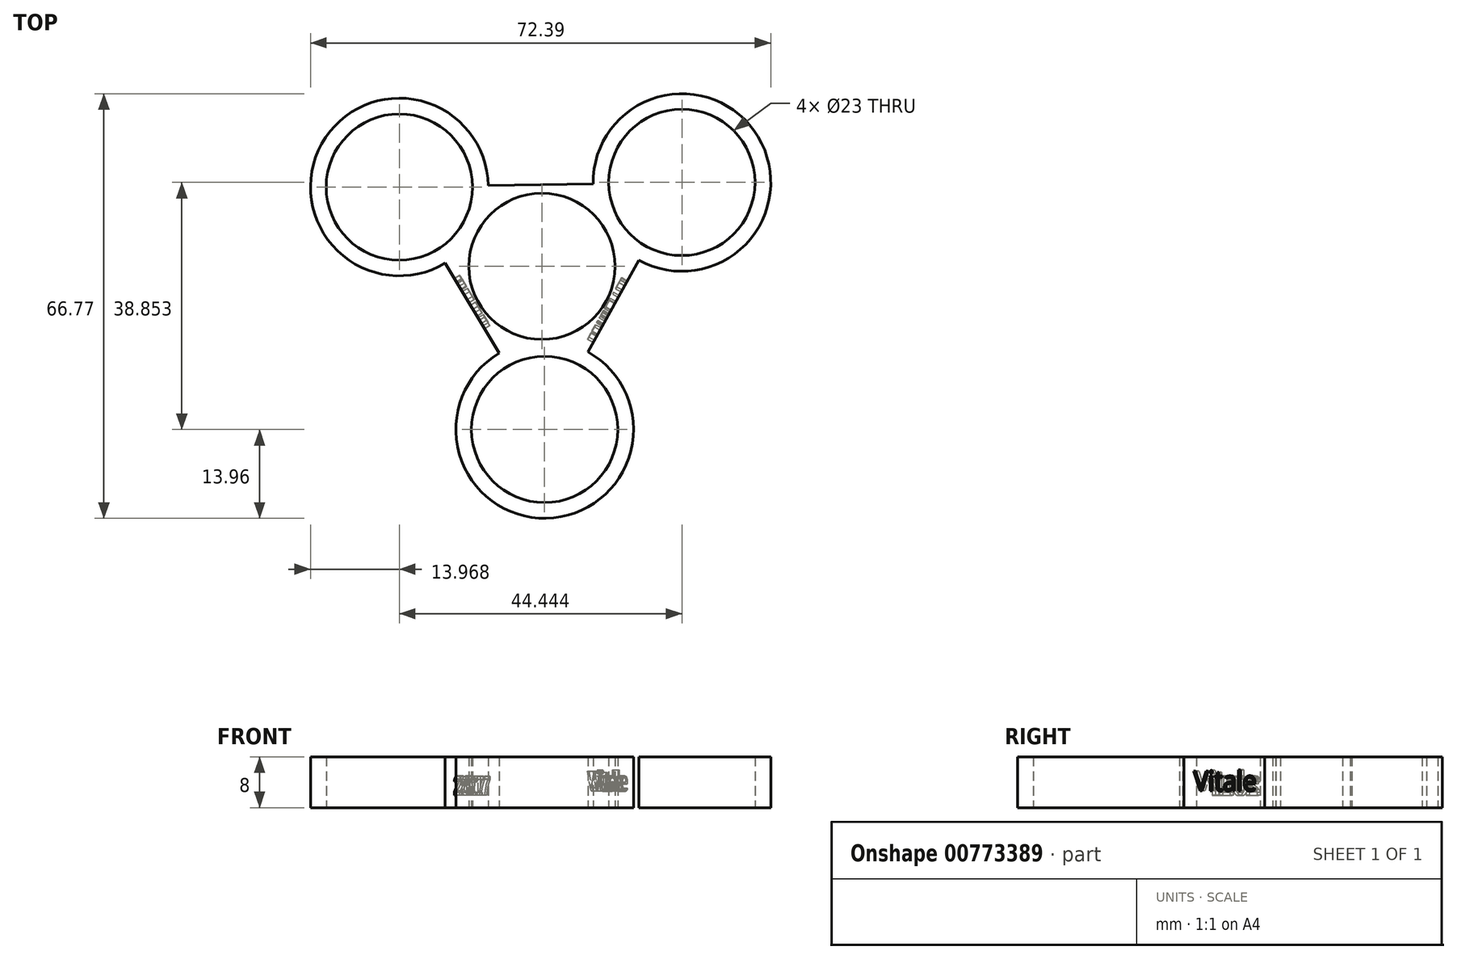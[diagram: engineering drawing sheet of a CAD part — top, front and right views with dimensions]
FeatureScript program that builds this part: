
annotation { "Feature Type Name" : "Feature", "Feature Type Description" : "" }
export const myFeature = defineFeature(function(context is Context, id is Id, definition is map)
    precondition{}
    {
        {
            var Q0;
            Q0=qCreatedBy(makeId("Top.planeOp"),FACE);
            var sketch = newSketch(context, id + "F0", { "sketchPlane" : qUnion([Q0])});
            skCircle(sketch, "E0", {"center": v(0.42, -25.66) * mm, "radius": 11.5 * mm});
            skCircle(sketch, "E1", {"center": v(-22.43, 12.47) * mm, "radius": 11.5 * mm});
            skCircle(sketch, "E2", {"center": v(22.01, 13.2) * mm, "radius": 11.5 * mm});
            skCircle(sketch, "E3", {"center": v(0, 0) * mm, "radius": 11.5 * mm});
            skSolve(sketch);
        }
        {
            var Q0;
            Q0=qCreatedBy(makeId("Top.planeOp"),FACE);
            var sketch = newSketch(context, id + "F1", { "sketchPlane" : qUnion([Q0])});
            skCircle(sketch, "E4", {"center": v(-22.43, 12.47) * mm, "radius": 13.97 * mm});
            skCircle(sketch, "E5", {"center": v(22.02, 13.18) * mm, "radius": 13.97 * mm});
            skCircle(sketch, "E6", {"center": v(0.43, -25.65) * mm, "radius": 13.97 * mm});
            skLineSegment(sketch, "E7", {"start": v(-22.43, 12.47) * mm, "end": v(0.43, -25.65) * mm});
            skLineSegment(sketch, "E8", {"start": v(0.43, -25.65) * mm, "end": v(22.02, 13.18) * mm});
            skLineSegment(sketch, "E9", {"start": v(22.02, 13.18) * mm, "end": v(-22.43, 12.47) * mm});
            skSolve(sketch);
        }
        {
            var Q0;
            Q0 = qSketchRegion(id + "F1", true);
            extrude(context, id + "F2", {"entities" : qUnion([Q0]), "endBound" : BoundingType.SYMMETRIC, "depth" : 8 * mm, "offsetDistance" : 25.4 * mm});
        }
        {
            var Q0;
            Q0 = qSketchRegion(id + "F0", true);
            extrude(context, id + "F3", {"entities" : qUnion([Q0]), "operationType" : NewBodyOperationType.REMOVE, "endBound" : BoundingType.SYMMETRIC, "depth" : 8 * mm, "offsetDistance" : 25.4 * mm});
        }
        {
            var Q0;
            Q0=makeQuery(id+"F2.opExtrude","SWEPT_FACE",FACE,{"disambiguationData":[OSD([sQuery(id+"F1.wireOp",EDGE,"E8")])]});
            var sketch = newSketch(context, id + "F4", { "sketchPlane" : qUnion([Q0])});
            skText(sketch, "E10", { "text": "Vitale", "fontName": "OpenSans-Regular.ttf"});
            const initialGuessF4  = {"E10": [-0.00653, -0.00136, 1, 0, 0.00316]};
            skSetInitialGuess(sketch, initialGuessF4);
            skSolve(sketch);
        }
        {
            var Q0;
            Q0 = qSketchRegion(id + "F4", true);
            extrude(context, id + "F5", {"entities" : qUnion([Q0]), "operationType" : NewBodyOperationType.REMOVE, "oppositeDirection" : true, "depth" : 1 * mm, "offsetDistance" : 25.4 * mm});
        }
        {
            var Q0;
            Q0=makeQuery(id+"F2.opExtrude","SWEPT_FACE",FACE,{"disambiguationData":[OSD([sQuery(id+"F1.wireOp",EDGE,"E7")])]});
            var sketch = newSketch(context, id + "F6", { "sketchPlane" : qUnion([Q0])});
            skText(sketch, "E11", { "text": "2017", "fontName": "Arimo-Bold.ttf"});
            const initialGuessF6  = {"E11": [-0.00558, -0.00204, 1, 0, 0.0031]};
            skSetInitialGuess(sketch, initialGuessF6);
            skSolve(sketch);
        }
        {
            var Q0;
            Q0 = qSketchRegion(id + "F6", true);
            extrude(context, id + "F7", {"entities" : qUnion([Q0]), "operationType" : NewBodyOperationType.REMOVE, "oppositeDirection" : true, "depth" : 1 * mm, "offsetDistance" : 25.4 * mm});
        }
    });
